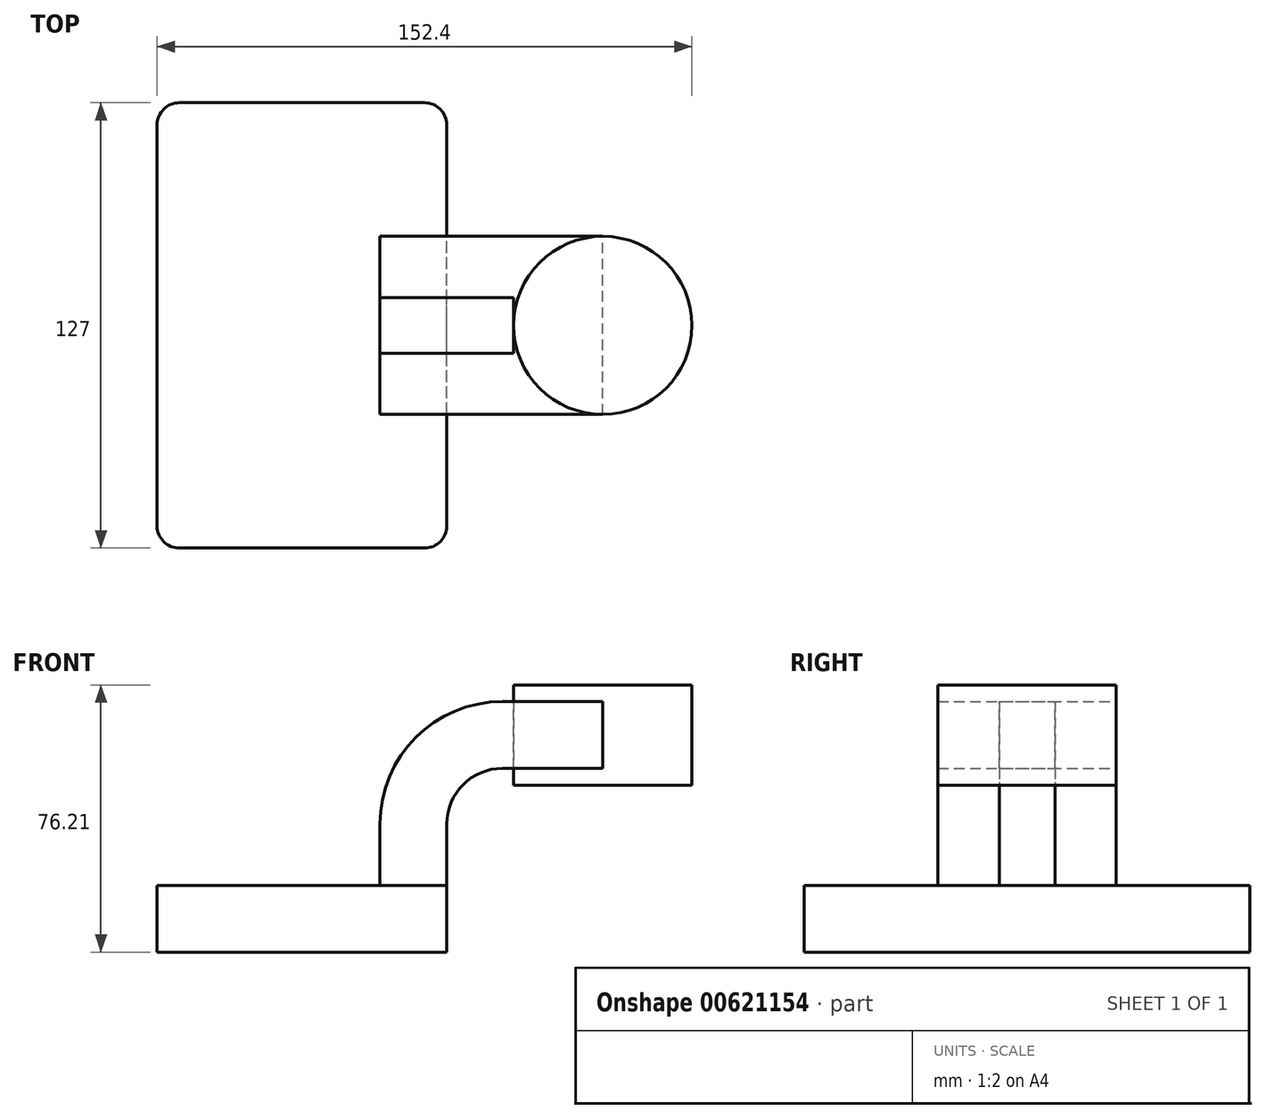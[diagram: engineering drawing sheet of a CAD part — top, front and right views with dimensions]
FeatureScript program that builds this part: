
annotation { "Feature Type Name" : "Feature", "Feature Type Description" : "" }
export const myFeature = defineFeature(function(context is Context, id is Id, definition is map)
    precondition{}
    {
        {
            var Q0;
            Q0=qCreatedBy(makeId("Front.planeOp"),FACE);
            var sketch = newSketch(context, id + "F0", { "sketchPlane" : qUnion([Q0])});
            skLineSegment(sketch, "E0.bottom", {"start": v(-41.28, 9.52) * mm, "end": v(41.28, 9.53) * mm});
            skLineSegment(sketch, "E0.top", {"start": v(-41.28, -9.52) * mm, "end": v(41.28, -9.52) * mm});
            skLineSegment(sketch, "E0.left", {"start": v(-41.28, 9.52) * mm, "end": v(-41.27, -9.53) * mm});
            skLineSegment(sketch, "E0.right", {"start": v(41.28, 9.53) * mm, "end": v(41.28, -9.52) * mm});
            skPoint(sketch, "E0.middle", {"position": v(0, 0) * mm});
            skLineSegment(sketch, "E1.bottom", {"start": v(111.12, 38.1) * mm, "end": v(60.32, 38.1) * mm});
            skLineSegment(sketch, "E1.top", {"start": v(111.12, 66.68) * mm, "end": v(60.32, 66.68) * mm});
            skLineSegment(sketch, "E1.left", {"start": v(111.12, 38.1) * mm, "end": v(111.12, 66.68) * mm});
            skLineSegment(sketch, "E1.right", {"start": v(60.32, 38.1) * mm, "end": v(60.32, 66.68) * mm});
            skPoint(sketch, "E1.middle", {"position": v(85.72, 52.39) * mm});
            skLineSegment(sketch, "E2", {"start": v(41.27, 9.53) * mm, "end": v(41.27, 27) * mm});
            skArc(sketch, "E3", {"start": v(41.27, 27) * mm, "mid": v(45.92, 38.23) * mm, "end": v(57.15, 42.88) * mm});
            skLineSegment(sketch, "E4", {"start": v(57.15, 42.88) * mm, "end": v(85.72, 42.88) * mm});
            skLineSegment(sketch, "E5.0", {"start": v(57.15, 61.93) * mm, "end": v(85.72, 61.93) * mm});
            skArc(sketch, "E5.1", {"start": v(22.23, 27) * mm, "mid": v(32.45, 51.7) * mm, "end": v(57.15, 61.93) * mm});
            skLineSegment(sketch, "E5.2", {"start": v(22.22, 9.53) * mm, "end": v(22.22, 27) * mm});
            skFitSpline(sketch, "E6", {"points": [v(-41.28, 9.52) * mm, v(57.15, 61.93) * mm], "startDerivative": vector(0.3, 95.96) * mm, "endDerivative": vector(87.75, -1.47) * mm});
            skLineSegment(sketch, "E7", {"start": v(85.72, 38.1) * mm, "end": v(85.72, 66.68) * mm});
            skSolve(sketch);
        }
        {
            var Q0;
            Q0=makeQuery(id+"F0.imprint","IMPRINT",FACE,{"disambiguationData":[TD([[makeQuery(id+"F0.imprint","IMPRINT",EDGE,{"derivedFrom":sQuery(id+"F0.wireOp",EDGE,"E0.top")}),1.0]])]});
            extrude(context, id + "F1", {"entities" : qUnion([Q0]), "endBound" : BoundingType.SYMMETRIC, "depth" : 127 * mm, "offsetDistance" : 25.4 * mm});
        }
        {
            var Q0;
            {var subQ1=sQuery(id+"F0.wireOp",EDGE,"E2");Q0=makeQuery(id+"F0.imprint","IMPRINT",FACE,{"disambiguationData":[TD([[makeQuery(id+"F0.imprint","IMPRINT",EDGE,{"derivedFrom":subQ1}),1.0]])]});}
            var Q1;
            {var subQ0=sQuery(id+"F0.wireOp",EDGE,"E4");var subQ1=sQuery(id+"F0.wireOp",EDGE,"E1.right");var subQ2=makeQuery(id+"F0.imprint","INTERSECT",VERTEX,{"derivedFrom":[subQ1,subQ0]});Q1=makeQuery(id+"F0.imprint","IMPRINT",FACE,{"disambiguationData":[TD([[makeQuery(id+"F0.imprint","IMPRINT",EDGE,{"disambiguationData":[TD([[subQ2,-1.0]])],"derivedFrom":subQ1}),-1.0]])]});}
            extrude(context, id + "F2", {"entities" : qUnion([Q0, Q1]), "endBound" : BoundingType.SYMMETRIC, "depth" : 50.8 * mm, "offsetDistance" : 25.4 * mm});
        }
        {
            var Q0;
            Q0=makeQuery(id+"F0.imprint","IMPRINT",FACE,{"disambiguationData":[TD([[makeQuery(id+"F0.imprint","IMPRINT",EDGE,{"derivedFrom":sQuery(id+"F0.wireOp",EDGE,"E5.1")}),1.0]])]});
            extrude(context, id + "F3", {"entities" : qUnion([Q0]), "endBound" : BoundingType.SYMMETRIC, "depth" : 15.88 * mm, "offsetDistance" : 25.4 * mm});
        }
        {
            var Q0;
            {var subQ0=sQuery(id+"F0.wireOp",EDGE,"E1.left");Q0=makeQuery(id+"F0.imprint","IMPRINT",FACE,{"disambiguationData":[TD([[makeQuery(id+"F0.imprint","IMPRINT",EDGE,{"derivedFrom":subQ0}),1.0]])]});}
            var Q1;
            Q1=sQuery(id+"F0.wireOp",EDGE,"E7");
            revolve(context, id + "F4", {"entities" : qUnion([Q0]), "axis" : qUnion([Q1]), "revolveType" : RevolveType.FULL});
        }
        {
            var Q0;
            Q0=makeQuery(id+"F1.opExtrude","CAP_EDGE",EDGE,{"disambiguationData":[OSD([sQuery(id+"F0.wireOp",EDGE,"E0.right")])],"isStart":false});
            var Q1;
            Q1=makeQuery(id+"F1.opExtrude","CAP_EDGE",EDGE,{"disambiguationData":[OSD([sQuery(id+"F0.wireOp",EDGE,"E0.left")])],"isStart":false});
            var Q2;
            Q2=makeQuery(id+"F1.opExtrude","CAP_EDGE",EDGE,{"disambiguationData":[OSD([sQuery(id+"F0.wireOp",EDGE,"E0.left")])],"isStart":true});
            var Q3;
            Q3=makeQuery(id+"F1.opExtrude","CAP_EDGE",EDGE,{"disambiguationData":[OSD([sQuery(id+"F0.wireOp",EDGE,"E0.right")])],"isStart":true});
            fillet(context, id + "F5", {"entities" : qUnion([Q0, Q1, Q2, Q3]), "radius" : 6.35 * mm, "tangentPropagation" : true, "allowEdgeOverflow" : false});
        }
    });
